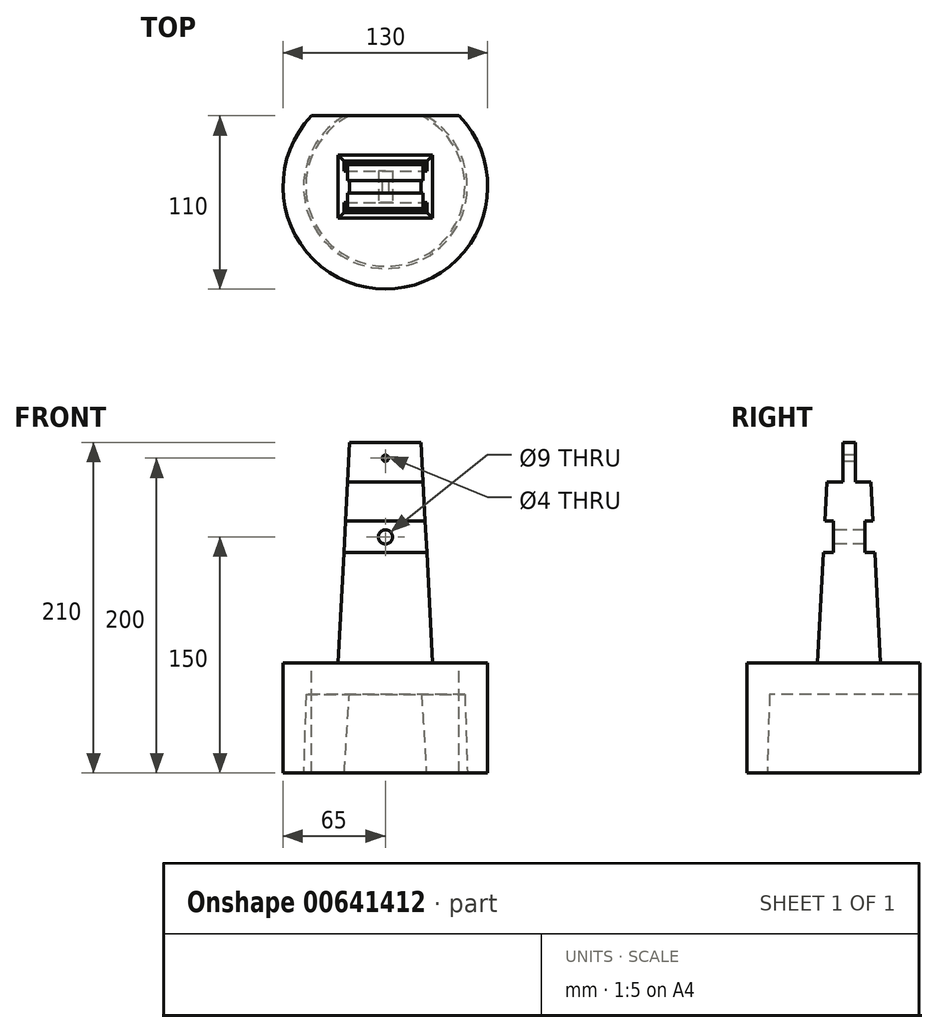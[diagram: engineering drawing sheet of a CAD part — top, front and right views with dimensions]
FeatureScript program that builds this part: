
annotation { "Feature Type Name" : "Feature", "Feature Type Description" : "" }
export const myFeature = defineFeature(function(context is Context, id is Id, definition is map)
    precondition{}
    {
        {
            var Q0;
            Q0=qCreatedBy(makeId("Right.planeOp"),FACE);
            var sketch = newSketch(context, id + "F0", { "sketchPlane" : qUnion([Q0])});
            skLineSegment(sketch, "E0", {"start": v(0, -6.71) * mm, "end": v(0, 114.7) * mm, "construction": true});
            skLineSegment(sketch, "E1", {"start": v(-52, 0) * mm, "end": v(-65, 0) * mm});
            skLineSegment(sketch, "E2", {"start": v(-65, 0) * mm, "end": v(-65, 70) * mm});
            skLineSegment(sketch, "E3", {"start": v(-65, 70) * mm, "end": v(0, 70) * mm});
            skLineSegment(sketch, "E4", {"start": v(-52, 0) * mm, "end": v(-50.5, 50) * mm});
            skLineSegment(sketch, "E5", {"start": v(-50.5, 50) * mm, "end": v(0, 50) * mm});
            skLineSegment(sketch, "E6", {"start": v(0, 70) * mm, "end": v(0, 50) * mm});
            skSolve(sketch);
        }
        {
            var Q0;
            Q0 = qSketchRegion(id + "F0", true);
            var Q1;
            Q1=sQuery(id+"F0.wireOp",EDGE,"E0");
            revolve(context, id + "F1", {"entities" : qUnion([Q0]), "axis" : qUnion([Q1]), "revolveType" : RevolveType.FULL});
        }
        {
            var Q0;
            Q0=makeQuery(id+"F1.opRevolve","SWEPT_FACE",FACE,{"disambiguationData":[OSD([sQuery(id+"F0.wireOp",EDGE,"E3")])]});
            var sketch = newSketch(context, id + "F2", { "sketchPlane" : qUnion([Q0])});
            skLineSegment(sketch, "E7.bottom", {"start": v(30, 20) * mm, "end": v(-30, 20) * mm});
            skLineSegment(sketch, "E7.top", {"start": v(30, -20) * mm, "end": v(-30, -20) * mm});
            skLineSegment(sketch, "E7.left", {"start": v(30, 20) * mm, "end": v(30, -20) * mm});
            skLineSegment(sketch, "E7.right", {"start": v(-30, 20) * mm, "end": v(-30, -20) * mm});
            skPoint(sketch, "E7.middle", {"position": v(0, 0) * mm});
            skSolve(sketch);
        }
        {
            var Q0;
            Q0 = qSketchRegion(id + "F2", true);
            extrude(context, id + "F3", {"entities" : qUnion([Q0]), "operationType" : NewBodyOperationType.ADD, "depth" : 140 * mm, "offsetDistance" : 25 * mm, "hasDraft" : true, "draftAngle" : 3 * degree, "draftPullDirection" : true});
        }
        {
            var Q0;
            Q0=qCreatedBy(makeId("Right.planeOp"),FACE);
            var sketch = newSketch(context, id + "F4", { "sketchPlane" : qUnion([Q0])});
            skLineSegment(sketch, "E8", {"start": v(0, 210) * mm, "end": v(0, 70) * mm, "construction": true});
            skLineSegment(sketch, "E9.bottom", {"start": v(-40, 160) * mm, "end": v(-10, 160) * mm});
            skLineSegment(sketch, "E9.top", {"start": v(-40, 140) * mm, "end": v(-10, 140) * mm});
            skLineSegment(sketch, "E9.left", {"start": v(-40, 160) * mm, "end": v(-40, 140) * mm});
            skLineSegment(sketch, "E9.right", {"start": v(-10, 160) * mm, "end": v(-10, 140) * mm});
            skLineSegment(sketch, "E10", {"start": v(-40, 150) * mm, "end": v(-64.05, 150) * mm, "construction": true});
            skLineSegment(sketch, "E11.bottom", {"start": v(10, 140) * mm, "end": v(40, 140) * mm});
            skLineSegment(sketch, "E11.top", {"start": v(10, 160) * mm, "end": v(40, 160) * mm});
            skLineSegment(sketch, "E11.left", {"start": v(10, 140) * mm, "end": v(10, 160) * mm});
            skLineSegment(sketch, "E11.right", {"start": v(40, 140) * mm, "end": v(40, 160) * mm});
            skSolve(sketch);
        }
        {
            var Q0;
            Q0 = qSketchRegion(id + "F4", true);
            extrude(context, id + "F5", {"entities" : qUnion([Q0]), "operationType" : NewBodyOperationType.REMOVE, "endBound" : BoundingType.SYMMETRIC, "oppositeDirection" : true, "depth" : 300 * mm, "offsetDistance" : 25 * mm});
        }
        {
            var Q0;
            Q0=makeQuery(id+"F5.boolean.opBoolean","COPY",FACE,{"derivedFrom":makeQuery(id+"F5.opExtrude","SWEPT_FACE",FACE,{"disambiguationData":[OSD([sQuery(id+"F4.wireOp",EDGE,"E9.right")])]})});
            var sketch = newSketch(context, id + "F6", { "sketchPlane" : qUnion([Q0])});
            skCircle(sketch, "E12", {"center": v(0, 150) * mm, "radius": 4.5 * mm});
            skLineSegment(sketch, "E13", {"start": v(0, 140) * mm, "end": v(0, 160) * mm, "construction": true});
            skLineSegment(sketch, "E14", {"start": v(0, 160) * mm, "end": v(0, 210.4) * mm, "construction": true});
            skCircle(sketch, "E15", {"center": v(0, 200) * mm, "radius": 2 * mm});
            skSolve(sketch);
        }
        {
            var Q0;
            Q0 = qSketchRegion(id + "F6", true);
            extrude(context, id + "F7", {"entities" : qUnion([Q0]), "operationType" : NewBodyOperationType.REMOVE, "endBound" : BoundingType.SYMMETRIC, "oppositeDirection" : true, "depth" : 300 * mm, "offsetDistance" : 25 * mm});
        }
        {
            var Q0;
            Q0=qCreatedBy(makeId("Right.planeOp"),FACE);
            var sketch = newSketch(context, id + "F8", { "sketchPlane" : qUnion([Q0])});
            skLineSegment(sketch, "E16", {"start": v(0, 0) * mm, "end": v(0, 134.5) * mm, "construction": true});
            skLineSegment(sketch, "E17.bottom", {"start": v(-4, 210) * mm, "end": v(-34, 210) * mm});
            skLineSegment(sketch, "E17.top", {"start": v(-4, 185) * mm, "end": v(-34, 185) * mm});
            skLineSegment(sketch, "E17.left", {"start": v(-4, 210) * mm, "end": v(-4, 185) * mm});
            skLineSegment(sketch, "E17.right", {"start": v(-34, 210) * mm, "end": v(-34, 185) * mm});
            skLineSegment(sketch, "E18.bottom", {"start": v(4, 210) * mm, "end": v(34, 210) * mm});
            skLineSegment(sketch, "E18.top", {"start": v(4, 185) * mm, "end": v(34, 185) * mm});
            skLineSegment(sketch, "E18.left", {"start": v(4, 210) * mm, "end": v(4, 185) * mm});
            skLineSegment(sketch, "E18.right", {"start": v(34, 210) * mm, "end": v(34, 185) * mm});
            skSolve(sketch);
        }
        {
            var Q0;
            Q0 = qSketchRegion(id + "F8", true);
            extrude(context, id + "F9", {"entities" : qUnion([Q0]), "operationType" : NewBodyOperationType.REMOVE, "endBound" : BoundingType.SYMMETRIC, "oppositeDirection" : true, "depth" : 300 * mm, "offsetDistance" : 25 * mm});
        }
        {
            var Q0;
            Q0=makeQuery(id+"F1.opRevolve","SWEPT_FACE",FACE,{"disambiguationData":[OSD([sQuery(id+"F0.wireOp",EDGE,"E3")])]});
            var sketch = newSketch(context, id + "F10", { "sketchPlane" : qUnion([Q0])});
            skLineSegment(sketch, "E19.bottom", {"start": v(-46.9, 45) * mm, "end": v(46.9, 45) * mm});
            skLineSegment(sketch, "E19.top", {"start": v(-46.9, 65) * mm, "end": v(46.9, 65) * mm});
            skLineSegment(sketch, "E19.left", {"start": v(-46.9, 45) * mm, "end": v(-46.9, 65) * mm});
            skLineSegment(sketch, "E19.right", {"start": v(46.9, 45) * mm, "end": v(46.9, 65) * mm});
            skSolve(sketch);
        }
        {
            var Q0;
            Q0 = qSketchRegion(id + "F10", true);
            extrude(context, id + "F11", {"entities" : qUnion([Q0]), "operationType" : NewBodyOperationType.REMOVE, "endBound" : BoundingType.THROUGH_ALL, "oppositeDirection" : true, "depth" : 25 * mm, "offsetDistance" : 25 * mm});
        }
    });
